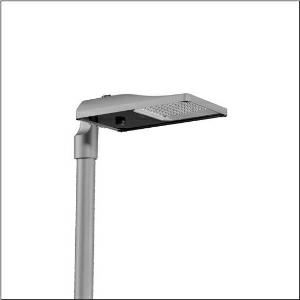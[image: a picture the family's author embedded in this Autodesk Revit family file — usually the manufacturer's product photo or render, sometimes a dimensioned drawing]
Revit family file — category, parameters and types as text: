
# Revit family: streetlight_sl_31_midi___st0_5a_5xh7b5at08qa_40ba
name_source: partatom
category: Lighting Fixtures
units: mm (PartAtom-declared; Revit-internal decimal feet)

## family parameters
Cut with Voids When Loaded = No
Host = Face
Light Source = No
Part Type = Normal
Room Calculation Point = No
Round Connector Dimension = Use Diameter
Shared = No

## types (1)
- --- (1 x LED, 21420 lm, 163.3 W, 3000K)
    Apparent Load = 163 VA
    CIE Flux Codes = 43 76 97 100 100
    Color Rendering = 80
    Color Temperature = 3000K
    Default Elevation = 1800 mm
    Description = Streetlight SL 31 midi D4i mast luminaire for post-top, side-entry; light control with lens of PMMA; light distribution: ST0.5a, direct asymmetric distribution, for standard-compliant lighting for roads and squares; LED: luminous flux: 21.420lm, light colour: 830, colour temperature: 3000K; luminous efficacy: 131,2lm/W; control: pre-setting: logarithmic dimming characteristic, flexible luminous flux parameterisation, time-dependent luminous flux control, constant luminous flux control, power reduction, intelligent temperature release in ECG and LED module, overheat protection; luminaire housing, of diecast aluminium, Siteco® metallic grey (DB 702S), corrosivity category C5 high according to DIN EN ISO 12944; cover of toughened safety glass, transparent, opened without tools; mast flange of diecast aluminium, Siteco® metallic grey (DB 702S), spigot size: 76/60mm, mast flange included unmounted; with cable H07RN-F 2x 1.5mm², cable length: 14,5m, connection cable pre-assembled; mains connection: 220..240V, AC, 50/60Hz; power consumption (at start of service life): 163,3W / (at end of service life): 178,2W / (with reduced operation 50%): 72,4W; protection rating (complete): IP66; insulation class (complete): insulation class II (safety insulation); impact resistance: IK09; certification: CE, ENEC, ENEC+, VDE, UKCA, ZD4i; permissible operating ambient temperature for outdoor applications: -40..+50°C; packaging unit: 1 piece

Light Distribution: ST0.5a
    Height = 79 mm
    Lamp = 1 x LED
    Lamp Light Flux = 21420 lm
    Lamp Power = 163.3 W
    Lamp count = 1
    Length = 577 mm
    Luminous efficacy = 131 lm/W
    Manufacturer = Siteco
    ModVariant = No
    Model = 5XH7B5AT08QA
    Number of Poles = 1
    OnlyDefault = Yes
    Power Factor = 1
    Product Name = Streetlight SL 31 midi | ST0.5a
    Product group = mast luminaire | pylon top
    ProductGroupID = 6100
    Protection Class = Protection class II
    Protection Degree = IP 66
    RLX_Detail_Level = 1
    RLX_Emergency_Light_Flux = 0 lm
    RLX_Emergency_Type = 0
    RLX_Emergency_Type_DB = No
    RlxData = <blob elided: 54301 chars, md5=380ad18e>
    Socket = socket
    Standby Power = 0 W
    System Light Flux = 21420 lm
    System Power = 163 W
    Type Comments = factory setting: luminous flux: 100 % | dim-lin: 254 | 865 mA
    Type Image = l_1300321.jpg
    URL = http://relux.com
    VarID = @adj_057486
    Voltage = 0 V
    Weight = 0.00 kg
    Width = 362 mm

## geometry (parser evidence)
native form markers: Blend x4, Sweep x12
no freeform markers — native parametric forms only
